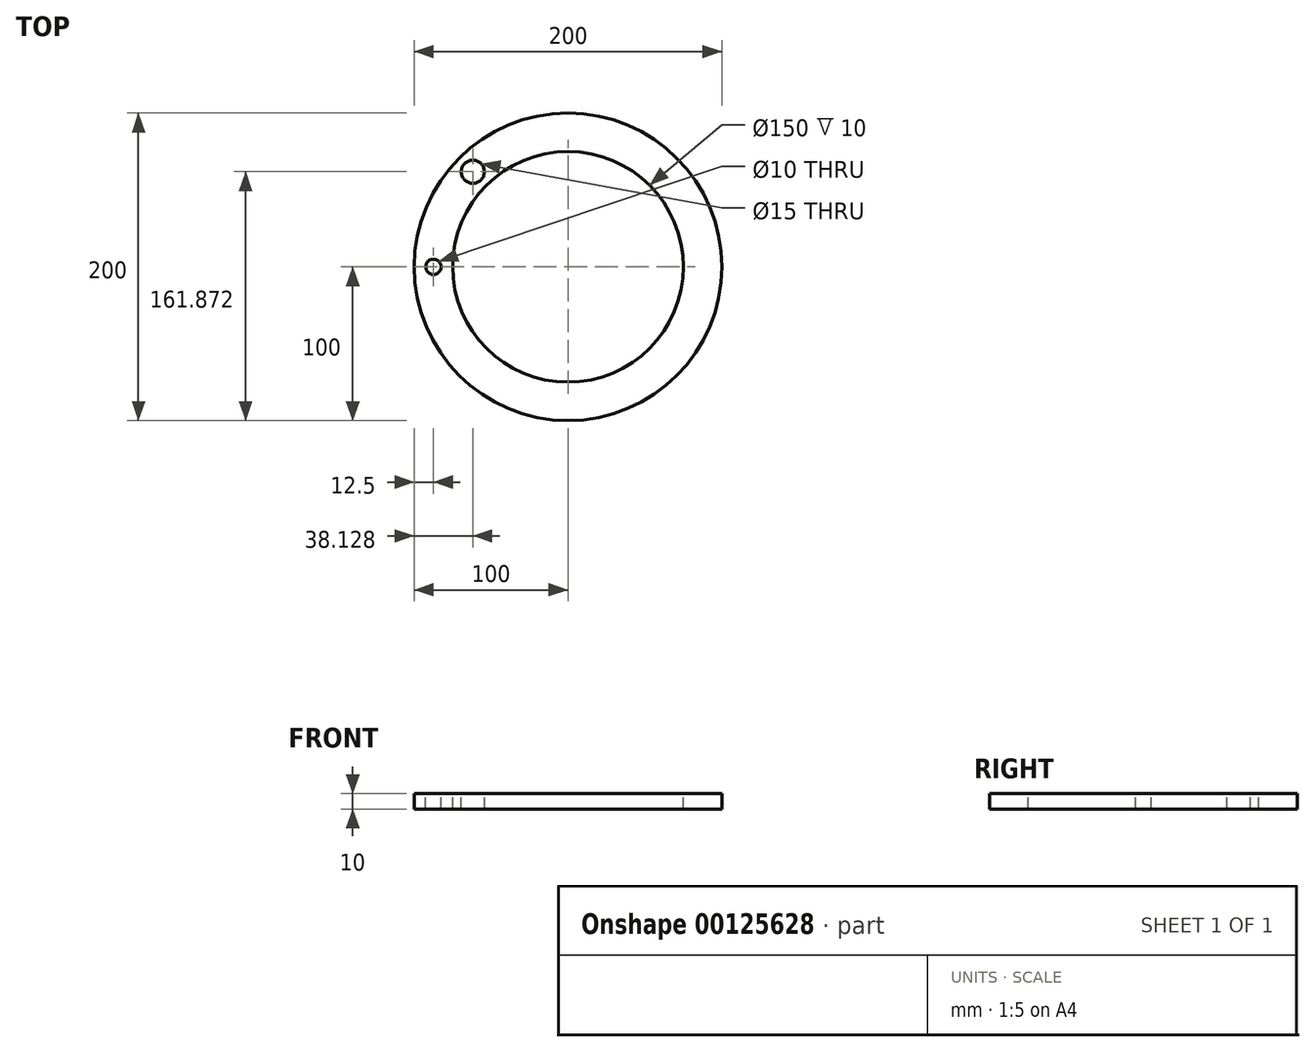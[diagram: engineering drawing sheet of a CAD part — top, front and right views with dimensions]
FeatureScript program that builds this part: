
annotation { "Feature Type Name" : "Feature", "Feature Type Description" : "" }
export const myFeature = defineFeature(function(context is Context, id is Id, definition is map)
    precondition{}
    {
        {
            var Q0;
            Q0=qCreatedBy(makeId("Top.planeOp"),FACE);
            var sketch = newSketch(context, id + "F0", { "sketchPlane" : qUnion([Q0])});
            skCircle(sketch, "E0", {"center": v(0, 0) * mm, "radius": 100 * mm});
            skSolve(sketch);
        }
        {
            var Q0;
            Q0 = qSketchRegion(id + "F0", true);
            extrude(context, id + "F1", {"entities" : qUnion([Q0]), "depth" : 10 * mm});
        }
        {
            var Q0;
            Q0=makeQuery(id+"F1.opExtrude","CAP_FACE",FACE,{"disambiguationData":[OSD([sQuery(id+"F0.wireOp",EDGE,"E0")])],"isStart":false});
            var sketch = newSketch(context, id + "F2", { "sketchPlane" : qUnion([Q0])});
            skCircle(sketch, "E1", {"center": v(0, 0) * mm, "radius": 75 * mm});
            skSolve(sketch);
        }
        {
            var Q0;
            Q0=makeQuery(id+"F2.imprint","IMPRINT",FACE,{"disambiguationData":[TD([[makeQuery(id+"F2.imprint","IMPRINT",EDGE,{"derivedFrom":sQuery(id+"F2.wireOp",EDGE,"E1")}),1.0]])]});
            extrude(context, id + "F3", {"entities" : qUnion([Q0]), "operationType" : NewBodyOperationType.REMOVE, "endBound" : BoundingType.THROUGH_ALL, "oppositeDirection" : true, "depth" : 25 * mm});
        }
        {
            var Q0;
            Q0=makeQuery(id+"F1.opExtrude","CAP_FACE",FACE,{"disambiguationData":[OSD([sQuery(id+"F0.wireOp",EDGE,"E0")])],"isStart":false});
            var sketch = newSketch(context, id + "F4", { "sketchPlane" : qUnion([Q0])});
            skCircle(sketch, "E2", {"center": v(-87.5, 0) * mm, "radius": 5 * mm});
            skSolve(sketch);
        }
        {
            var Q0;
            Q0=makeQuery(id+"F4.imprint","IMPRINT",FACE,{"disambiguationData":[TD([[makeQuery(id+"F4.imprint","IMPRINT",EDGE,{"derivedFrom":sQuery(id+"F4.wireOp",EDGE,"E2")}),1.0]])]});
            extrude(context, id + "F5", {"entities" : qUnion([Q0]), "operationType" : NewBodyOperationType.REMOVE, "endBound" : BoundingType.THROUGH_ALL, "oppositeDirection" : true, "depth" : 25 * mm});
        }
        {
            var Q0;
            Q0=qCreatedBy(makeId("Front.planeOp"),FACE);
            var sketch = newSketch(context, id + "F6", { "sketchPlane" : qUnion([Q0])});
            skLineSegment(sketch, "E3", {"start": v(0, -73.28) * mm, "end": v(0, 69.32) * mm, "construction": true});
            skSolve(sketch);
        }
        {
            var Q0;
            Q0=qCreatedBy(makeId("Right.planeOp"),FACE);
            var Q1;
            Q1=qCreatedBy(makeId("Front.planeOp"),FACE);
            cPlane(context, id + "F7", {"entities" : qUnion([Q0, Q1]), "cplaneType" : CPlaneType.MID_PLANE, "offset" : 25 * mm, "width" : 150 * mm, "height" : 150 * mm});
        }
        {
            var Q0;
            Q0=makeQuery(id+"F1.opExtrude","CAP_FACE",FACE,{"disambiguationData":[OSD([sQuery(id+"F0.wireOp",EDGE,"E0")])],"isStart":false});
            var sketch = newSketch(context, id + "F8", { "sketchPlane" : qUnion([Q0])});
            skCircle(sketch, "E4", {"center": v(-61.87, 61.87) * mm, "radius": 7.5 * mm});
            skSolve(sketch);
        }
        {
            var Q0;
            Q0=makeQuery(id+"F8.imprint","IMPRINT",FACE,{"disambiguationData":[TD([[makeQuery(id+"F8.imprint","IMPRINT",EDGE,{"derivedFrom":sQuery(id+"F8.wireOp",EDGE,"E4")}),1.0]])]});
            extrude(context, id + "F9", {"entities" : qUnion([Q0]), "operationType" : NewBodyOperationType.REMOVE, "endBound" : BoundingType.THROUGH_ALL, "oppositeDirection" : true, "depth" : 25 * mm});
        }
    });
